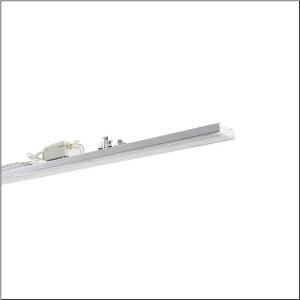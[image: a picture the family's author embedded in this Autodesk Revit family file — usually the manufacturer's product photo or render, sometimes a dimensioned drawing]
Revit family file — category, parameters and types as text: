
# Revit family: licross_21_recessed_ho_52te1ecn4cxs
name_source: partatom
category: Lighting Fixtures
units: mm (PartAtom-declared; Revit-internal decimal feet)

## family parameters
Cut with Voids When Loaded = No
Host = Face
Light Source = No
Part Type = Normal
Room Calculation Point = No
Round Connector Dimension = Use Diameter
Shared = No

## types (1)
- --- (1 x LED, 12350 lm, 68.4 W, 4000K)
    Apparent Load = 68 VA
    CIE Flux Codes = 85 95 99 100 100
    Color Rendering = 80
    Color Temperature = 4000K
    Default Elevation = 1800 mm
    Description = Licross 21 Recessed HO, luminaire insert, of sheet steel, galvanised, coil coated, white, length: 1.500mm, width: 66mm, height: 67mm, LED rated luminous flux: 12.350lm, light colour: 840, SDCM (Standard Deviation of Colour Matching)MacAdam ≤ 3 SDCM (initial), control gear: ON/OFF Multilumen, CLOi, with plug, 3-pole, with phase selection, mains connection: 220..240V, AC, 50/60Hz, start of lifetime: 69W, end of service life: 83W, internal wiring halogen-free, primary light control with lens, of plastic, primary optical cover: cover, of PMMA, light emission: direct distribution, primary light characteristic: symmetric, protection rating (complete): IP54, insulation class (complete): insulation class I (protective earthing), certification: CE, ENEC, VDE, UKCA, protection symbol: D if used in an environment with non-conductive dust loads with corresponding accessories, impact resistance: IK06, permissible ambient temperature for indoor applications: -35..+30°C, corresponds to IFS (International Featured Standards) requirements for safety and quality in the food industry, reducing of maximum allowable ambient temperature of 5°C with ceiling mounting, LABS conformity tested according to VDMA 24364:2018-05, The light source and the operating device comply with the requirements of the Ecodesign Regulation (EU) 2019/2020 and are replaceable in accordance with this regulation, packaging unit: 1 piece
    Height = 58 mm
    Lamp = 1 x LED
    Lamp Light Flux = 12350 lm
    Lamp Power = 68.4 W
    Lamp count = 1
    Length = 1500 mm
    Luminous efficacy = 181 lm/W
    Manufacturer = Siteco
    ModVariant = No
    Model = 52TE1ECN4CXS
    Mounting Place = Ceiling
    Mounting Type = Pendant
    Number of Poles = 1
    OnlyDefault = Yes
    Power Factor = 1
    Product Name = Licross 21 Recessed HO
    Product group = luminaire insert | ceiling pendant
    ProductGroupID = 901
    Protection Class = Protection class I
    Protection Degree = IP 54
    RLX_Detail_Level = 1
    RLX_Emergency_Light_Flux = 0 lm
    RLX_Emergency_Type = 0
    RLX_Emergency_Type_DB = No
    RlxData = <blob elided: 22721 chars, md5=43eb30ce>
    Socket = socket
    Standby Power = 0 W
    System Light Flux = 12350 lm
    System Power = 68 W
    Type Comments = factory setting: luminous flux: 100 % | (A | C | E) | 161 mA
    Type Image = l_1296930.jpg
    URL = http://relux.com
    VarID = @adj_111365
    Voltage = 0 V
    Weight = 0.00 kg
    Width = 66 mm

## geometry (parser evidence)
native form markers: Blend x4, Sweep x12
no freeform markers — native parametric forms only
